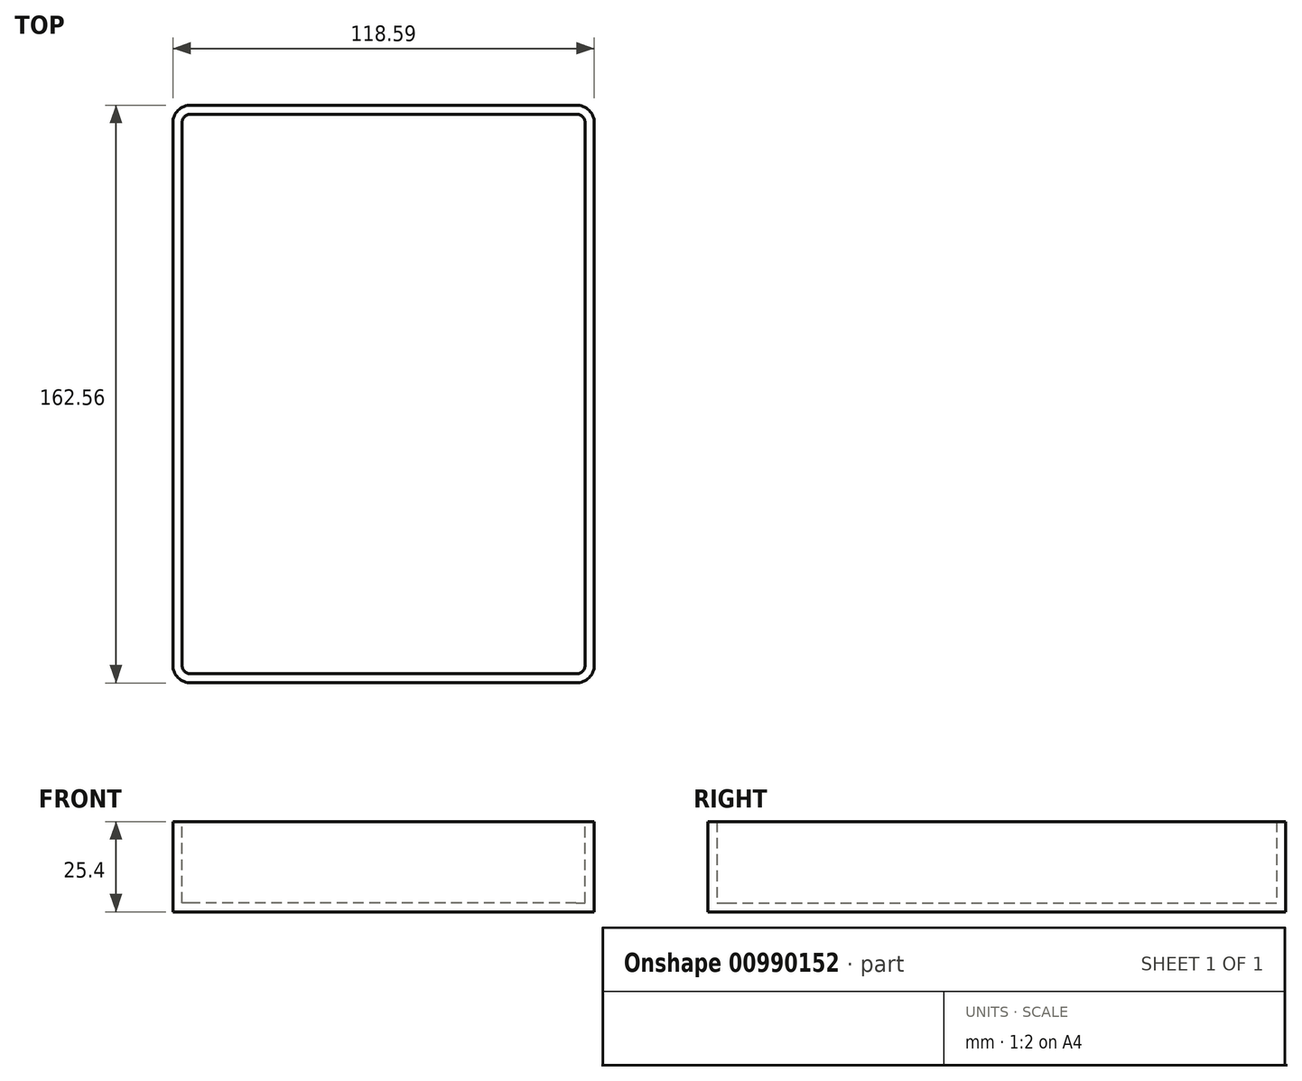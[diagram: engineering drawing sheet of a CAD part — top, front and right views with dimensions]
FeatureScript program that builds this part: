
annotation { "Feature Type Name" : "Feature", "Feature Type Description" : "" }
export const myFeature = defineFeature(function(context is Context, id is Id, definition is map)
    precondition{}
    {
        {
            var Q0;
            Q0=qCreatedBy(makeId("Top.planeOp"),FACE);
            var sketch = newSketch(context, id + "F0", { "sketchPlane" : qUnion([Q0])});
            skLineSegment(sketch, "E0.bottom", {"start": v(118.59, -23.3) * mm, "end": v(0, -23.3) * mm});
            skLineSegment(sketch, "E0.top", {"start": v(118.59, 139.25) * mm, "end": v(0, 139.25) * mm});
            skLineSegment(sketch, "E0.left", {"start": v(118.59, -23.3) * mm, "end": v(118.59, 139.25) * mm});
            skLineSegment(sketch, "E0.right", {"start": v(0, -23.3) * mm, "end": v(0, 139.25) * mm});
            skSolve(sketch);
        }
        {
            var Q0;
            Q0 = qSketchRegion(id + "F0", true);
            extrude(context, id + "F1", {"entities" : qUnion([Q0]), "depth" : 25.4 * mm, "offsetDistance" : 25.4 * mm});
        }
        {
            var Q0;
            Q0=makeQuery(id+"F1.opExtrude","SWEPT_EDGE",EDGE,{"disambiguationData":[OSD([sQuery(id+"F0.wireOp",EDGE,"E0.bottom"),sQuery(id+"F0.wireOp",EDGE,"E0.left")])]});
            var Q1;
            Q1=makeQuery(id+"F1.opExtrude","SWEPT_EDGE",EDGE,{"disambiguationData":[OSD([sQuery(id+"F0.wireOp",EDGE,"E0.top"),sQuery(id+"F0.wireOp",EDGE,"E0.left")])]});
            var Q2;
            Q2=makeQuery(id+"F1.opExtrude","SWEPT_EDGE",EDGE,{"disambiguationData":[OSD([sQuery(id+"F0.wireOp",EDGE,"E0.top"),sQuery(id+"F0.wireOp",EDGE,"E0.right")])]});
            var Q3;
            Q3=makeQuery(id+"F1.opExtrude","SWEPT_EDGE",EDGE,{"disambiguationData":[OSD([sQuery(id+"F0.wireOp",EDGE,"E0.bottom"),sQuery(id+"F0.wireOp",EDGE,"E0.right")])]});
            fillet(context, id + "F2", {"entities" : qUnion([Q0, Q1, Q2, Q3]), "radius" : 5.08 * mm, "tangentPropagation" : true, "allowEdgeOverflow" : false});
        }
        {
            var Q0;
            Q0=makeQuery(id+"F1.opExtrude","CAP_FACE",FACE,{"disambiguationData":[OSD([sQuery(id+"F0.wireOp",EDGE,"E0.bottom"),sQuery(id+"F0.wireOp",EDGE,"E0.top"),sQuery(id+"F0.wireOp",EDGE,"E0.left"),sQuery(id+"F0.wireOp",EDGE,"E0.right")])],"isStart":false});
            shell(context, id + "F3", {"entities" : qUnion([Q0]), "thickness" : 2.54 * mm});
        }
    });
